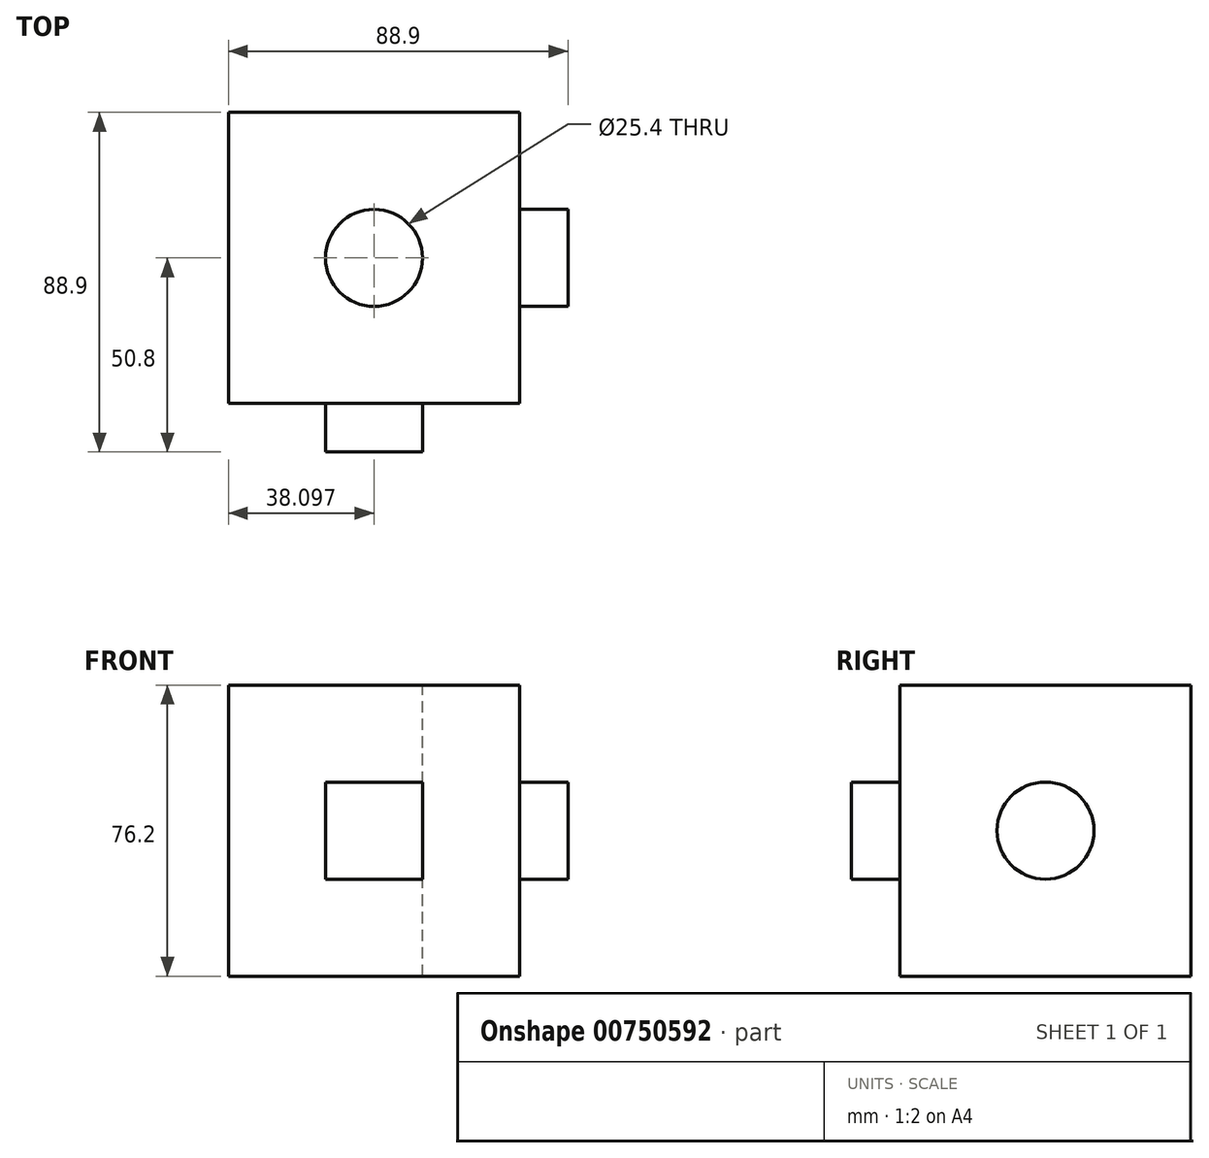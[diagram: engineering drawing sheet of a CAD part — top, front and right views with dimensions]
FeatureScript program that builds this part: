
annotation { "Feature Type Name" : "Feature", "Feature Type Description" : "" }
export const myFeature = defineFeature(function(context is Context, id is Id, definition is map)
    precondition{}
    {
        {
            var Q0;
            Q0=qCreatedBy(makeId("Front.planeOp"),FACE);
            var sketch = newSketch(context, id + "F0", { "sketchPlane" : qUnion([Q0])});
            skLineSegment(sketch, "E0.bottom", {"start": v(-41.32, 55.02) * mm, "end": v(34.88, 55.02) * mm});
            skLineSegment(sketch, "E0.top", {"start": v(-41.32, -21.18) * mm, "end": v(34.88, -21.18) * mm});
            skLineSegment(sketch, "E0.left", {"start": v(-41.32, 55.02) * mm, "end": v(-41.32, -21.18) * mm});
            skLineSegment(sketch, "E0.right", {"start": v(34.88, 55.02) * mm, "end": v(34.88, -21.18) * mm});
            skSolve(sketch);
        }
        {
            var Q0;
            Q0=makeQuery(id+"F0.imprint","IMPRINT",FACE,{"disambiguationData":[TD([[makeQuery(id+"F0.imprint","IMPRINT",EDGE,{"derivedFrom":sQuery(id+"F0.wireOp",EDGE,"E0.bottom")}),-1.0]])]});
            extrude(context, id + "F1", {"entities" : qUnion([Q0]), "depth" : 76.2 * mm, "offsetDistance" : 25.4 * mm});
        }
        {
            var Q0;
            Q0=makeQuery(id+"F1.opExtrude","CAP_FACE",FACE,{"disambiguationData":[OSD([sQuery(id+"F0.wireOp",EDGE,"E0.bottom"),sQuery(id+"F0.wireOp",EDGE,"E0.top"),sQuery(id+"F0.wireOp",EDGE,"E0.left"),sQuery(id+"F0.wireOp",EDGE,"E0.right")])],"isStart":false});
            var sketch = newSketch(context, id + "F2", { "sketchPlane" : qUnion([Q0])});
            skLineSegment(sketch, "E1.bottom", {"start": v(-15.92, 29.62) * mm, "end": v(9.48, 29.62) * mm});
            skLineSegment(sketch, "E1.top", {"start": v(-15.92, 4.22) * mm, "end": v(9.48, 4.22) * mm});
            skLineSegment(sketch, "E1.left", {"start": v(-15.92, 29.62) * mm, "end": v(-15.92, 4.22) * mm});
            skLineSegment(sketch, "E1.right", {"start": v(9.48, 29.62) * mm, "end": v(9.48, 4.22) * mm});
            skLineSegment(sketch, "E2.bottom", {"start": v(-3.22, 29.62) * mm, "end": v(-2.96, 29.62) * mm});
            skLineSegment(sketch, "E2.top", {"start": v(-3.22, 29.62) * mm, "end": v(-2.96, 29.62) * mm});
            skLineSegment(sketch, "E2.left", {"start": v(-3.22, 29.62) * mm, "end": v(-3.22, 29.62) * mm});
            skLineSegment(sketch, "E2.right", {"start": v(-2.96, 29.62) * mm, "end": v(-2.96, 29.62) * mm});
            skSolve(sketch);
        }
        {
            var Q0;
            Q0=makeQuery(id+"F2.imprint","IMPRINT",FACE,{"disambiguationData":[TD([[makeQuery(id+"F2.imprint","IMPRINT",EDGE,{"derivedFrom":sQuery(id+"F2.wireOp",EDGE,"E1.top")}),1.0]])]});
            extrude(context, id + "F3", {"entities" : qUnion([Q0]), "operationType" : NewBodyOperationType.ADD, "depth" : 12.7 * mm, "offsetDistance" : 25.4 * mm});
        }
        {
            var Q0;
            Q0=makeQuery(id+"F1.opExtrude","SWEPT_FACE",FACE,{"disambiguationData":[OSD([sQuery(id+"F0.wireOp",EDGE,"E0.right")])]});
            var sketch = newSketch(context, id + "F4", { "sketchPlane" : qUnion([Q0])});
            skCircle(sketch, "E3", {"center": v(-38.1, 16.92) * mm, "radius": 12.7 * mm});
            skSolve(sketch);
        }
        {
            var Q0;
            Q0=makeQuery(id+"F4.imprint","IMPRINT",FACE,{"disambiguationData":[TD([[makeQuery(id+"F4.imprint","IMPRINT",EDGE,{"derivedFrom":sQuery(id+"F4.wireOp",EDGE,"E3")}),1.0]])]});
            extrude(context, id + "F5", {"entities" : qUnion([Q0]), "operationType" : NewBodyOperationType.ADD, "depth" : 12.7 * mm, "offsetDistance" : 25.4 * mm});
        }
        {
            var Q0;
            Q0=makeQuery(id+"F1.opExtrude","SWEPT_FACE",FACE,{"disambiguationData":[OSD([sQuery(id+"F0.wireOp",EDGE,"E0.bottom")])]});
            var sketch = newSketch(context, id + "F6", { "sketchPlane" : qUnion([Q0])});
            skPoint(sketch, "E4", {"position": v(-3.22, -38.1) * mm});
            skSolve(sketch);
        }
        {
            var Q0;
            Q0=sQuery(id+"F6.wireOp",VERTEX,"E4");
            var Q1;
            Q1=makeQuery(id+"F1.opExtrude","SWEPT_BODY",BODY,{"disambiguationData":[OSD([sQuery(id+"F0.wireOp",EDGE,"E0.bottom"),sQuery(id+"F0.wireOp",EDGE,"E0.top"),sQuery(id+"F0.wireOp",EDGE,"E0.left"),sQuery(id+"F0.wireOp",EDGE,"E0.right")])]});
            hole(context, id + "F7", {"style" : HoleStyle.SIMPLE, "endStyle" : HoleEndStyle.THROUGH, "holeDiameter" : 25.4 * mm, "majorDiameter" : 6.35 * mm, "isTappedThrough" : true, "tappedDepth" : 12.7 * mm, "tapClearance" : 3, "locations" : qUnion([Q0]), "scope" : qUnion([Q1])});
        }
    });
